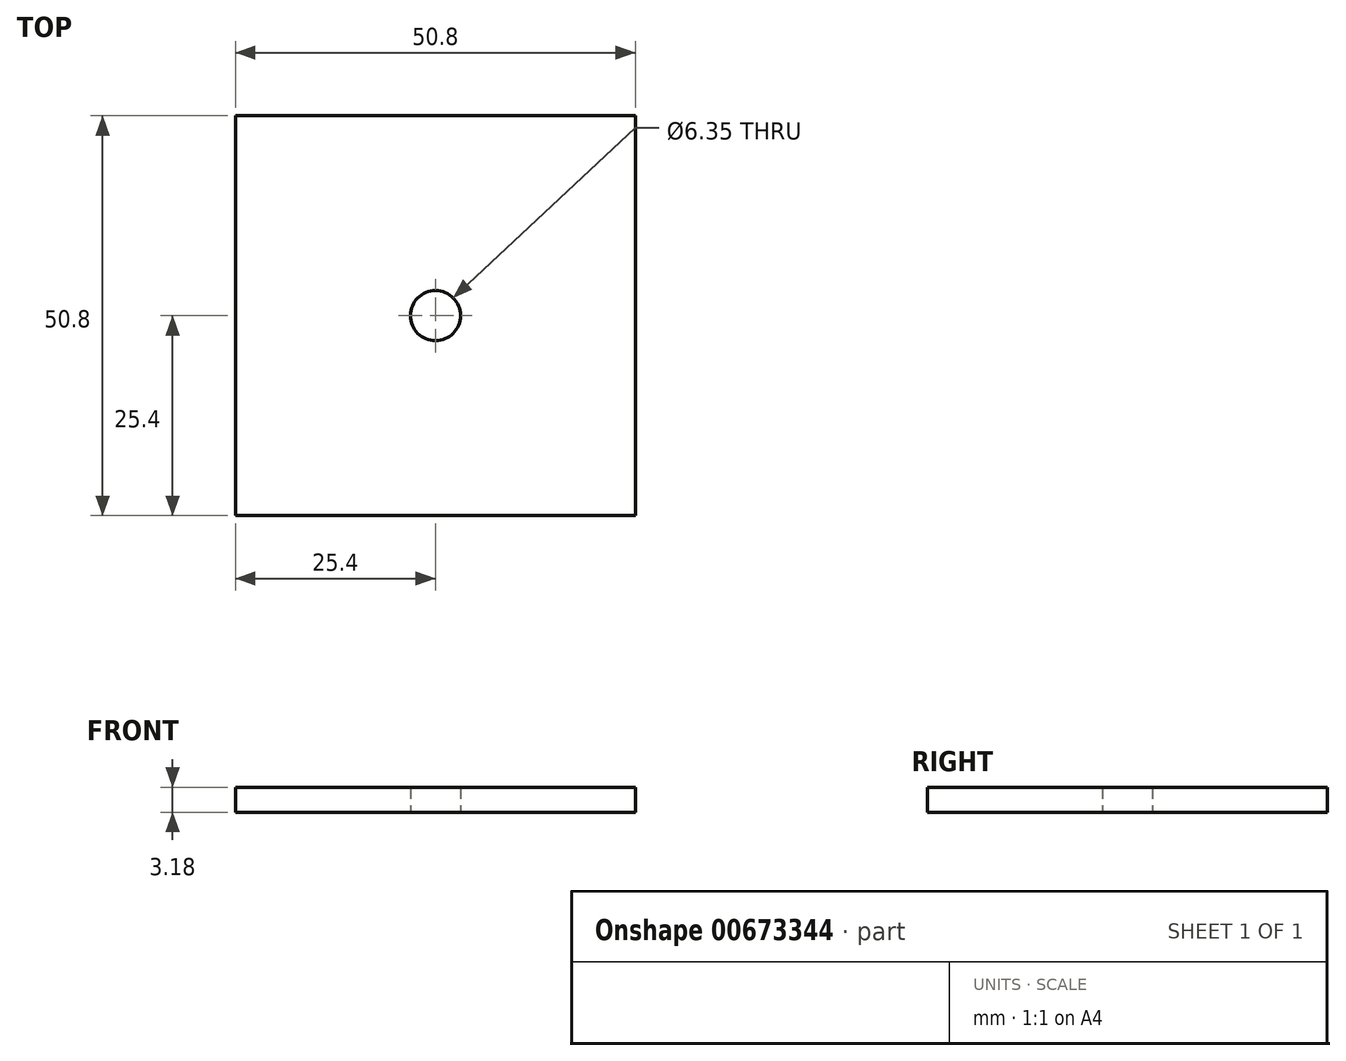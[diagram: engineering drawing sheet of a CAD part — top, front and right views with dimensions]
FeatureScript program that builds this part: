
annotation { "Feature Type Name" : "Feature", "Feature Type Description" : "" }
export const myFeature = defineFeature(function(context is Context, id is Id, definition is map)
    precondition{}
    {
        {
            var Q0;
            Q0=qCreatedBy(makeId("Top.planeOp"),FACE);
            var sketch = newSketch(context, id + "F0", { "sketchPlane" : qUnion([Q0])});
            skLineSegment(sketch, "E0.bottom", {"start": v(25.4, 25.4) * mm, "end": v(-25.4, 25.4) * mm});
            skLineSegment(sketch, "E0.top", {"start": v(25.4, -25.4) * mm, "end": v(-25.4, -25.4) * mm});
            skLineSegment(sketch, "E0.left", {"start": v(25.4, 25.4) * mm, "end": v(25.4, -25.4) * mm});
            skLineSegment(sketch, "E0.right", {"start": v(-25.4, 25.4) * mm, "end": v(-25.4, -25.4) * mm});
            skPoint(sketch, "E0.middle", {"position": v(0, 0) * mm});
            skCircle(sketch, "E1", {"center": v(0, 0) * mm, "radius": 3.18 * mm});
            skSolve(sketch);
        }
        {
            var Q0;
            Q0 = qSketchRegion(id + "F0", true);
            extrude(context, id + "F1", {"entities" : qUnion([Q0]), "depth" : 3.17 * mm, "offsetDistance" : 25.4 * mm});
        }
    });
